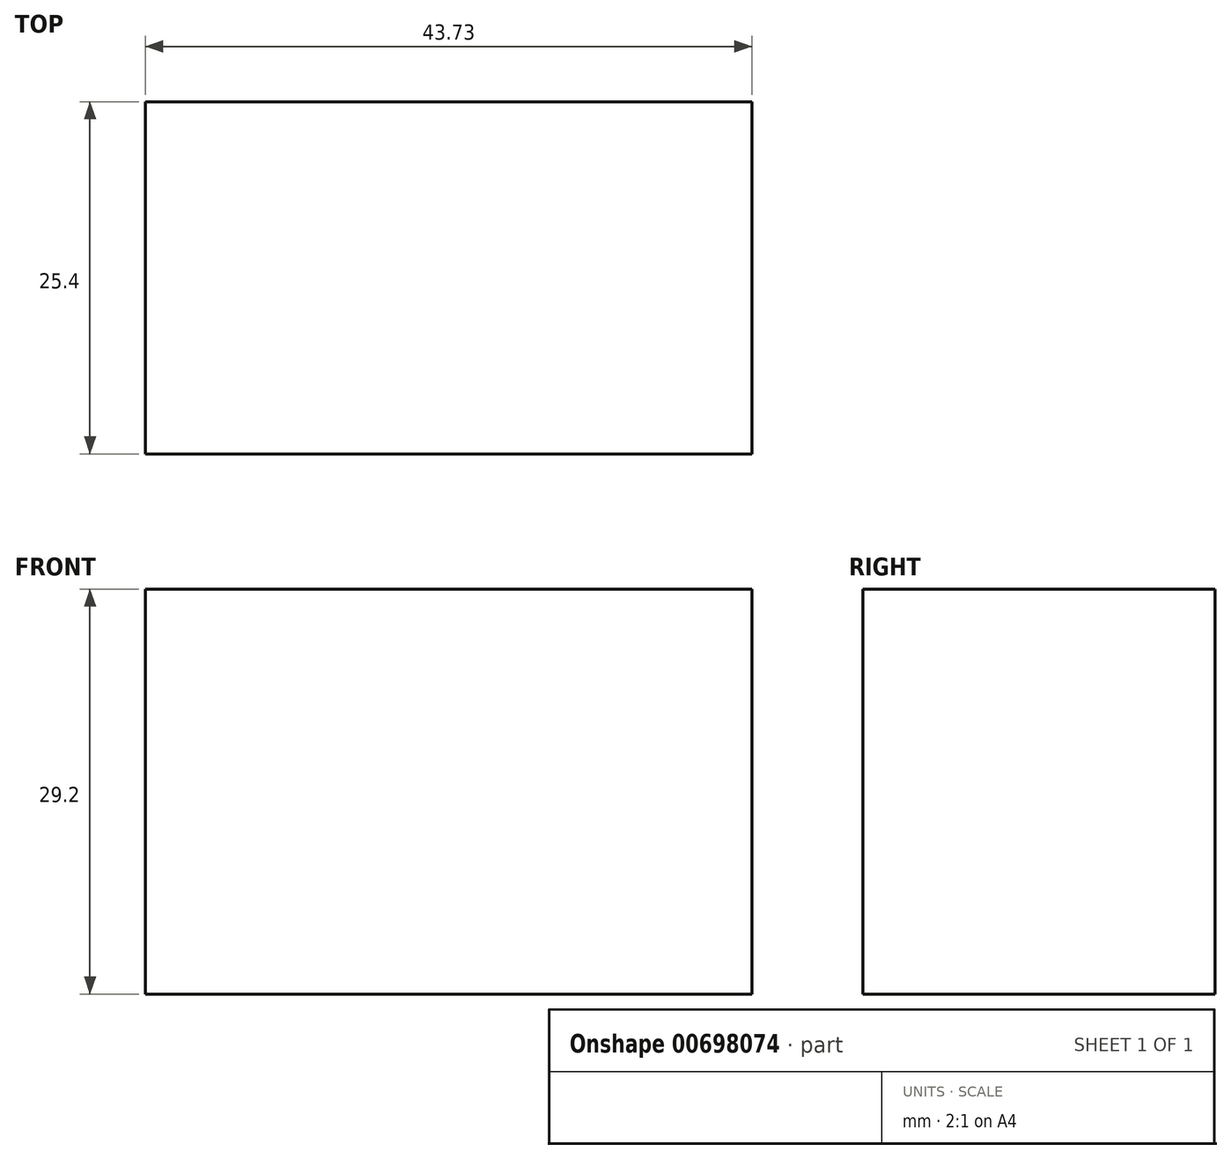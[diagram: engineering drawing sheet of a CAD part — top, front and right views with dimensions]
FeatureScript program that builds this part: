
annotation { "Feature Type Name" : "Feature", "Feature Type Description" : "" }
export const myFeature = defineFeature(function(context is Context, id is Id, definition is map)
    precondition{}
    {
        {
            var Q0;
            Q0=qCreatedBy(makeId("Front.planeOp"),FACE);
            var sketch = newSketch(context, id + "F0", { "sketchPlane" : qUnion([Q0])});
            skLineSegment(sketch, "E0.bottom", {"start": v(0, 0) * mm, "end": v(43.73, 0) * mm});
            skLineSegment(sketch, "E0.top", {"start": v(0, 29.2) * mm, "end": v(43.73, 29.2) * mm});
            skLineSegment(sketch, "E0.left", {"start": v(0, 0) * mm, "end": v(0, 29.2) * mm});
            skLineSegment(sketch, "E0.right", {"start": v(43.73, 0) * mm, "end": v(43.73, 29.2) * mm});
            skSolve(sketch);
        }
        {
            var Q0;
            Q0=makeQuery(id+"F0.imprint","IMPRINT",FACE,{"disambiguationData":[TD([[makeQuery(id+"F0.imprint","IMPRINT",EDGE,{"derivedFrom":sQuery(id+"F0.wireOp",EDGE,"E0.bottom")}),1.0]])]});
            extrude(context, id + "F1", {"entities" : qUnion([Q0]), "depth" : 25.4 * mm, "offsetDistance" : 25.4 * mm});
        }
    });
